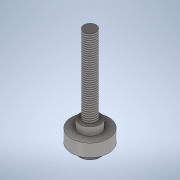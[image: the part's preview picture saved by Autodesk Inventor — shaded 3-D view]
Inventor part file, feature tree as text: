
AUTODESK INVENTOR PART (.ipt)
format: ipt  version: 2021 (Build 250183000, 183)  size: 120,832 bytes
history: native  units: mm
features: revolve x1, thread x1, sketch x1
ambient origin geometry x8: Origin, YZ Plane, XZ Plane, XY Plane, X Axis, Y Axis, Z Axis, Center Point
bodies: Solid1 (feature_tree)
feature tree (3):
  revolve  "Revolution1"  [1 undecoded]
  thread  "Thread1"  [1 undecoded]
  sketch  "Sketch1"  dims[d0=4.0mm d2=68.95mm d3=8.12mm d4=5.13mm d5=5.13mm d6=11.99mm d7=6.5mm d8=90.0deg d9=50.57mm d10=0.0mm]
note: 2 required parameter values undecoded (feature->parameter linkage not recoverable at this tier; creation-order binding heuristic only, values carry confidence <= 0.55)